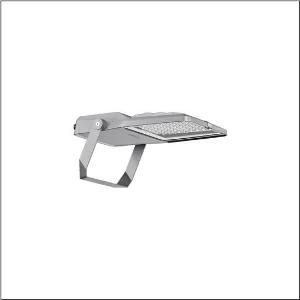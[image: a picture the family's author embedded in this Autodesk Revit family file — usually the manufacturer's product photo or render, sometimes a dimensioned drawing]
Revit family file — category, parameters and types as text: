
# Revit family: floodlight_fl_21_iq_mini___pl64_5xa7771d2e1a_0f9a
name_source: partatom
category: Lighting Fixtures
units: mm (PartAtom-declared; Revit-internal decimal feet)

## family parameters
Cut with Voids When Loaded = No
Host = Face
Light Source = No
Part Type = Normal
Room Calculation Point = No
Round Connector Dimension = Use Diameter
Shared = No

## types (1)
- --- (1 x LED, 17220 lm, 143 W, 3000K)
    Apparent Load = 143 VA
    CIE Flux Codes = 28 80 98 100 100
    Color Rendering = 70
    Color Temperature = 3000K
    Default Elevation = 1800 mm
    Description = Floodlight FL 21 iQ mini, floodlight, primary light control with lens, of PMMA, primary optical cover: protective disc, of toughened safety glass, transparent, light distribution: PL64, light emission: direct distribution, installation type: surface-mounted, LED, High Power LED, rated luminous flux: 17.220lm, luminous efficacy: 120lm/W, light colour: 730, colour temperature: 3000K, control: Auto-Match, Temp-Guard, Lumen-Switch, Night-Set, Smart-Wire, Light-Fading, Desk-Remote (wireless, voltage-free reading and setting of iQ features in the workshop via application-optimized NFC function/RFID function), optimised constant luminous flux control (CLO 2.0), with terminal, 6-pole, mains connection: 220..240V, AC, 50/60Hz, start of lifetime: 143W, end of service life: 152W, reduction: 61W, luminaire housing, of diecast aluminium, powder-coated, Siteco® metallic grey (DB 702S), corrosivity category C5 mid according to DIN EN ISO 12944, sealing non-destructively replaceable, mounting bracket, of steel, galvanised, powder-coated, Siteco® metallic grey (DB 702S), protection rating (complete): IP66, insulation class (complete): insulation class II (safety insulation), certification: CE, ENEC, VDE, protection symbol: D, impact resistance: IK08, permissible operating ambient temperature: -40..+40°C, permissible operating ambient temperature for outdoor applications: -40..+50°C, standard: DIN EN 12944, LABS conformity tested according to VDMA 24364:2018-05, packaging unit: 1 piece

Light Distribution: PL64
    Height = 70 mm
    Lamp = 1 x LED
    Lamp Light Flux = 17220 lm
    Lamp Power = 143 W
    Lamp count = 1
    Length = 485 mm
    Luminous efficacy = 120 lm/W
    Manufacturer = Siteco
    ModVariant = No
    Model = 5XA7771D2E1A
    Number of Poles = 1
    OnlyDefault = Yes
    Power Factor = 1
    Product Name = Floodlight FL 21 iQ mini | PL64
    Product group = floodlight | pylon annexe
    ProductGroupID = 6200
    Protection Class = Protection class II
    Protection Degree = IP 66
    RLX_Detail_Level = 1
    RLX_Emergency_Light_Flux = 0 lm
    RLX_Emergency_Type = 0
    RLX_Emergency_Type_DB = No
    RlxData = <blob elided: 96421 chars, md5=ed970d2c>
    Socket = socket
    Standby Power = 0 W
    System Light Flux = 17220 lm
    System Power = 143 W
    Type Comments = factory setting: luminous flux: 100 % | dim-lin: 254 | 730 mA
    Type Image = l_1006845.jpg
    URL = http://relux.com
    VarID = @adj_116295
    Voltage = 0 V
    Weight = 0.00 kg
    Width = 337 mm

## geometry (parser evidence)
native form markers: Blend x4, Sweep x13
no freeform markers — native parametric forms only
